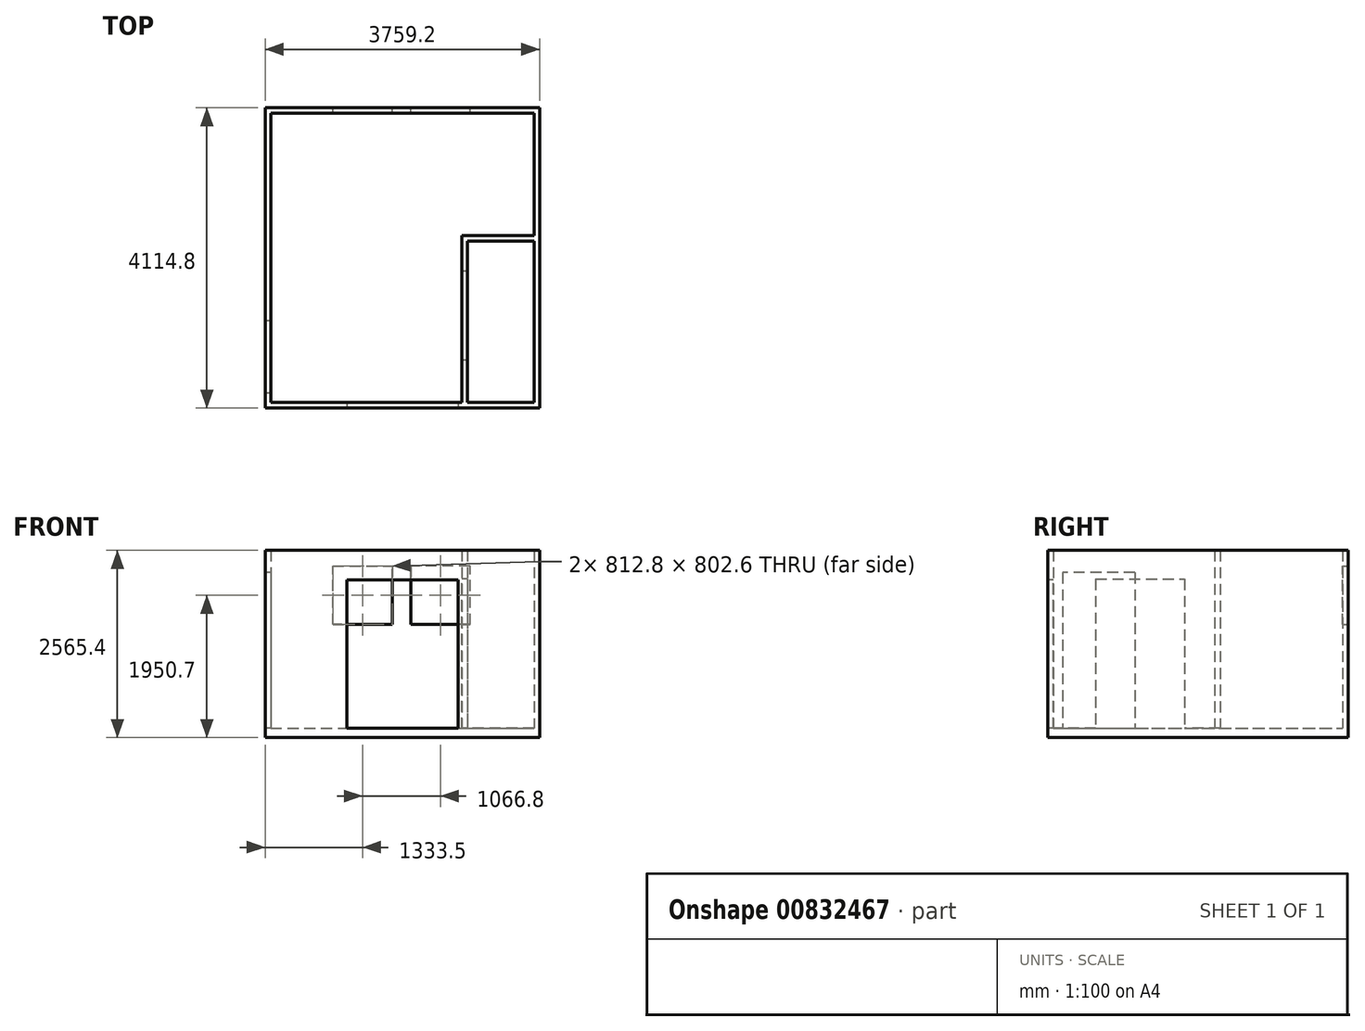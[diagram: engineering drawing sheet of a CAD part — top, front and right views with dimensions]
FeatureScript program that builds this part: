
annotation { "Feature Type Name" : "Feature", "Feature Type Description" : "" }
export const myFeature = defineFeature(function(context is Context, id is Id, definition is map)
    precondition{}
    {
        {
            var Q0;
            Q0=qCreatedBy(makeId("Top.planeOp"),FACE);
            var sketch = newSketch(context, id + "F0", { "sketchPlane" : qUnion([Q0])});
            skLineSegment(sketch, "E0.bottom", {"start": v(0, 0) * mm, "end": v(3606.8, 0) * mm});
            skLineSegment(sketch, "E0.top", {"start": v(0, 3962.4) * mm, "end": v(3606.8, 3962.4) * mm});
            skLineSegment(sketch, "E0.left", {"start": v(0, 0) * mm, "end": v(0, 3962.4) * mm});
            skLineSegment(sketch, "E0.right", {"start": v(3606.8, 0) * mm, "end": v(3606.8, 3962.4) * mm});
            skLineSegment(sketch, "E1.0", {"start": v(-76.2, -76.2) * mm, "end": v(-76.2, 4038.6) * mm});
            skLineSegment(sketch, "E1.1", {"start": v(-76.2, -76.2) * mm, "end": v(3683, -76.2) * mm});
            skLineSegment(sketch, "E1.2", {"start": v(3683, -76.2) * mm, "end": v(3683, 4038.6) * mm});
            skLineSegment(sketch, "E1.3", {"start": v(-76.2, 4038.6) * mm, "end": v(3683, 4038.6) * mm});
            skSolve(sketch);
        }
        {
            var Q0;
            Q0 = qSketchRegion(id + "F0", true);
            extrude(context, id + "F1", {"entities" : qUnion([Q0]), "depth" : 2438.4 * mm, "offsetDistance" : 25.4 * mm});
        }
        {
            var Q0;
            Q0=makeQuery(id+"F1.opExtrude","SWEPT_FACE",FACE,{"disambiguationData":[OSD([sQuery(id+"F0.wireOp",EDGE,"E1.0")])]});
            var sketch = newSketch(context, id + "F2", { "sketchPlane" : qUnion([Q0])});
            skLineSegment(sketch, "E2.bottom", {"start": v(-127, 0) * mm, "end": v(-1117.6, 0) * mm});
            skLineSegment(sketch, "E2.top", {"start": v(-127, 2133.6) * mm, "end": v(-1117.6, 2133.6) * mm});
            skLineSegment(sketch, "E2.left", {"start": v(-127, 0) * mm, "end": v(-127, 2133.6) * mm});
            skLineSegment(sketch, "E2.right", {"start": v(-1117.6, 0) * mm, "end": v(-1117.6, 2133.6) * mm});
            skSolve(sketch);
        }
        {
            var Q0;
            Q0 = qSketchRegion(id + "F2", true);
            var Q1;
            Q1=makeQuery(id+"F1.opExtrude","SWEPT_FACE",FACE,{"disambiguationData":[OSD([sQuery(id+"F0.wireOp",EDGE,"E0.left")])]});
            extrude(context, id + "F3", {"entities" : qUnion([Q0]), "operationType" : NewBodyOperationType.REMOVE, "endBound" : BoundingType.UP_TO_SURFACE, "oppositeDirection" : true, "depth" : 25.4 * mm, "endBoundEntityFace" : qUnion([Q1]), "offsetDistance" : 25.4 * mm});
        }
        {
            var Q0;
            Q0=makeQuery(id+"F1.opExtrude","SWEPT_FACE",FACE,{"disambiguationData":[OSD([sQuery(id+"F0.wireOp",EDGE,"E1.3")])]});
            var sketch = newSketch(context, id + "F4", { "sketchPlane" : qUnion([Q0])});
            skLineSegment(sketch, "E3.bottom", {"start": v(-1663.7, 2225) * mm, "end": v(-850.9, 2225) * mm});
            skLineSegment(sketch, "E3.top", {"start": v(-1663.7, 1422.4) * mm, "end": v(-850.9, 1422.4) * mm});
            skLineSegment(sketch, "E3.left", {"start": v(-1663.7, 2225) * mm, "end": v(-1663.7, 1422.4) * mm});
            skLineSegment(sketch, "E3.right", {"start": v(-850.9, 2225) * mm, "end": v(-850.9, 1422.4) * mm});
            skLineSegment(sketch, "E4.bottom", {"start": v(-1917.7, 2225) * mm, "end": v(-2730.5, 2225) * mm});
            skLineSegment(sketch, "E4.top", {"start": v(-1917.7, 1422.4) * mm, "end": v(-2730.5, 1422.4) * mm});
            skLineSegment(sketch, "E4.left", {"start": v(-1917.7, 2225) * mm, "end": v(-1917.7, 1422.4) * mm});
            skLineSegment(sketch, "E4.right", {"start": v(-2730.5, 2225) * mm, "end": v(-2730.5, 1422.4) * mm});
            skSolve(sketch);
        }
        {
            var Q0;
            Q0 = qSketchRegion(id + "F4", true);
            var Q1;
            Q1=makeQuery(id+"F1.opExtrude","SWEPT_FACE",FACE,{"disambiguationData":[OSD([sQuery(id+"F0.wireOp",EDGE,"E0.top")])]});
            extrude(context, id + "F5", {"entities" : qUnion([Q0]), "operationType" : NewBodyOperationType.REMOVE, "endBound" : BoundingType.UP_TO_SURFACE, "oppositeDirection" : true, "depth" : 25.4 * mm, "endBoundEntityFace" : qUnion([Q1]), "offsetDistance" : 25.4 * mm});
        }
        {
            var Q0;
            Q0=makeQuery(id+"F1.opExtrude","SWEPT_FACE",FACE,{"disambiguationData":[OSD([sQuery(id+"F0.wireOp",EDGE,"E1.1")])]});
            var sketch = newSketch(context, id + "F6", { "sketchPlane" : qUnion([Q0])});
            skLineSegment(sketch, "E5.bottom", {"start": v(1041.4, 0) * mm, "end": v(2565.4, 0) * mm});
            skLineSegment(sketch, "E5.top", {"start": v(1041.4, 2032) * mm, "end": v(2565.4, 2032) * mm});
            skLineSegment(sketch, "E5.left", {"start": v(1041.4, 0) * mm, "end": v(1041.4, 2032) * mm});
            skLineSegment(sketch, "E5.right", {"start": v(2565.4, 0) * mm, "end": v(2565.4, 2032) * mm});
            skSolve(sketch);
        }
        {
            var Q0;
            Q0 = qSketchRegion(id + "F6", true);
            extrude(context, id + "F7", {"entities" : qUnion([Q0]), "operationType" : NewBodyOperationType.REMOVE, "endBound" : BoundingType.UP_TO_NEXT, "oppositeDirection" : true, "depth" : 25.4 * mm, "offsetDistance" : 25.4 * mm});
        }
        {
            var Q0;
            Q0=qCreatedBy(makeId("Top.planeOp"),FACE);
            var sketch = newSketch(context, id + "F8", { "sketchPlane" : qUnion([Q0])});
            skLineSegment(sketch, "E6.0", {"start": v(-76.2, -76.2) * mm, "end": v(3683, -76.2) * mm});
            skLineSegment(sketch, "E7.0", {"start": v(-76.2, -76.2) * mm, "end": v(-76.2, 4038.6) * mm});
            skLineSegment(sketch, "E8.0", {"start": v(3683, -76.2) * mm, "end": v(3683, 4038.6) * mm});
            skLineSegment(sketch, "E9.0", {"start": v(-76.2, 4038.6) * mm, "end": v(3683, 4038.6) * mm});
            skSolve(sketch);
        }
        {
            var Q0;
            Q0 = qSketchRegion(id + "F8", true);
            extrude(context, id + "F9", {"entities" : qUnion([Q0]), "operationType" : NewBodyOperationType.ADD, "oppositeDirection" : true, "depth" : 127 * mm, "offsetDistance" : 25.4 * mm});
        }
        {
            var Q0;
            Q0=makeQuery(id+"F9.opExtrude","CAP_FACE",FACE,{"disambiguationData":[OSD([sQuery(id+"F8.wireOp",EDGE,"E6.0"),sQuery(id+"F8.wireOp",EDGE,"E7.0"),sQuery(id+"F8.wireOp",EDGE,"E8.0"),sQuery(id+"F8.wireOp",EDGE,"E9.0")])],"isStart":true});
            var sketch = newSketch(context, id + "F10", { "sketchPlane" : qUnion([Q0])});
            skLineSegment(sketch, "E10.0", {"start": v(3606.8, 0) * mm, "end": v(3606.8, 3962.4) * mm, "construction": true});
            skLineSegment(sketch, "E11.0", {"start": v(0, 0) * mm, "end": v(3606.8, 0) * mm, "construction": true});
            skLineSegment(sketch, "E12.0", {"start": v(0, 3962.4) * mm, "end": v(3606.8, 3962.4) * mm, "construction": true});
            skLineSegment(sketch, "E13", {"start": v(2692.4, 0) * mm, "end": v(2692.4, 2209.8) * mm});
            skLineSegment(sketch, "E14", {"start": v(3606.8, 2209.8) * mm, "end": v(2692.4, 2209.8) * mm});
            skLineSegment(sketch, "E15", {"start": v(3606.8, 2209.8) * mm, "end": v(3606.8, 2286) * mm});
            skLineSegment(sketch, "E16", {"start": v(3606.8, 2286) * mm, "end": v(2616.2, 2286) * mm});
            skLineSegment(sketch, "E17", {"start": v(2616.2, 2286) * mm, "end": v(2616.2, 0) * mm});
            skLineSegment(sketch, "E18", {"start": v(2692.4, 0) * mm, "end": v(2616.2, 0) * mm});
            skSolve(sketch);
        }
        {
            var Q0;
            Q0 = qSketchRegion(id + "F10", true);
            extrude(context, id + "F11", {"entities" : qUnion([Q0]), "operationType" : NewBodyOperationType.ADD, "depth" : 2438.4 * mm, "offsetDistance" : 25.4 * mm});
        }
        {
            var Q0;
            Q0=makeQuery(id+"F11.opExtrude","SWEPT_FACE",FACE,{"disambiguationData":[OSD([sQuery(id+"F10.wireOp",EDGE,"E17")])]});
            var sketch = newSketch(context, id + "F12", { "sketchPlane" : qUnion([Q0])});
            skLineSegment(sketch, "E19.0", {"start": v(-2286, 0) * mm, "end": v(0, 0) * mm, "construction": true});
            skLineSegment(sketch, "E20.bottom", {"start": v(-1799.58, 0) * mm, "end": v(-580.38, 0) * mm});
            skLineSegment(sketch, "E20.top", {"start": v(-1799.58, 2044.7) * mm, "end": v(-580.38, 2044.7) * mm});
            skLineSegment(sketch, "E20.left", {"start": v(-1799.58, 0) * mm, "end": v(-1799.58, 2044.7) * mm});
            skLineSegment(sketch, "E20.right", {"start": v(-580.38, 0) * mm, "end": v(-580.38, 2044.7) * mm});
            skSolve(sketch);
        }
        {
            var Q0;
            Q0 = qSketchRegion(id + "F12", true);
            extrude(context, id + "F13", {"entities" : qUnion([Q0]), "operationType" : NewBodyOperationType.REMOVE, "endBound" : BoundingType.UP_TO_NEXT, "oppositeDirection" : true, "depth" : 25.4 * mm, "offsetDistance" : 25.4 * mm});
        }
    });
